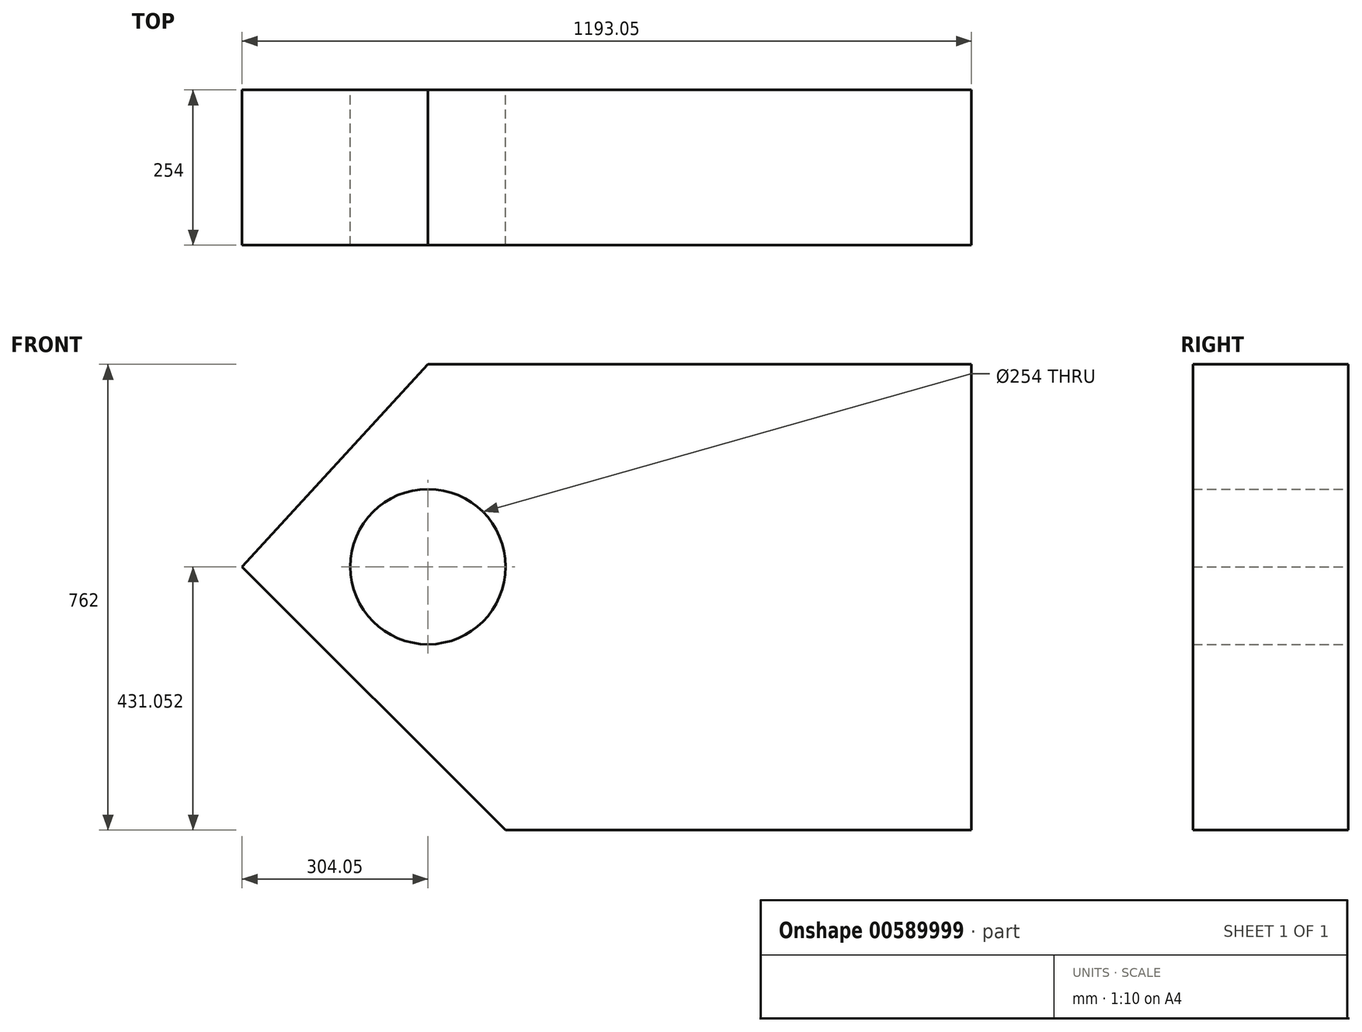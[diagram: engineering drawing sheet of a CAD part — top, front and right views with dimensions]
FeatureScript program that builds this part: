
annotation { "Feature Type Name" : "Feature", "Feature Type Description" : "" }
export const myFeature = defineFeature(function(context is Context, id is Id, definition is map)
    precondition{}
    {
        {
            var Q0;
            Q0=qCreatedBy(makeId("Front.planeOp"),FACE);
            var sketch = newSketch(context, id + "F0", { "sketchPlane" : qUnion([Q0])});
            skLineSegment(sketch, "E0", {"start": v(0, 0) * mm, "end": v(0, 762) * mm});
            skLineSegment(sketch, "E1", {"start": v(0, 762) * mm, "end": v(-889, 762) * mm});
            skLineSegment(sketch, "E2", {"start": v(0, 0) * mm, "end": v(-762, 0) * mm});
            skLineSegment(sketch, "E3", {"start": v(-762, 0) * mm, "end": v(-1193.05, 431.05) * mm});
            skLineSegment(sketch, "E4", {"start": v(-1193.05, 431.05) * mm, "end": v(-889, 762) * mm});
            skCircle(sketch, "E5", {"center": v(-889, 431.05) * mm, "radius": 127 * mm});
            skSolve(sketch);
        }
        {
            var Q0;
            Q0=makeQuery(id+"F0.imprint","IMPRINT",FACE,{"disambiguationData":[TD([[makeQuery(id+"F0.imprint","IMPRINT",EDGE,{"derivedFrom":sQuery(id+"F0.wireOp",EDGE,"E0")}),1.0]])]});
            extrude(context, id + "F1", {"entities" : qUnion([Q0]), "depth" : 254 * mm, "offsetDistance" : 25.4 * mm});
        }
    });
